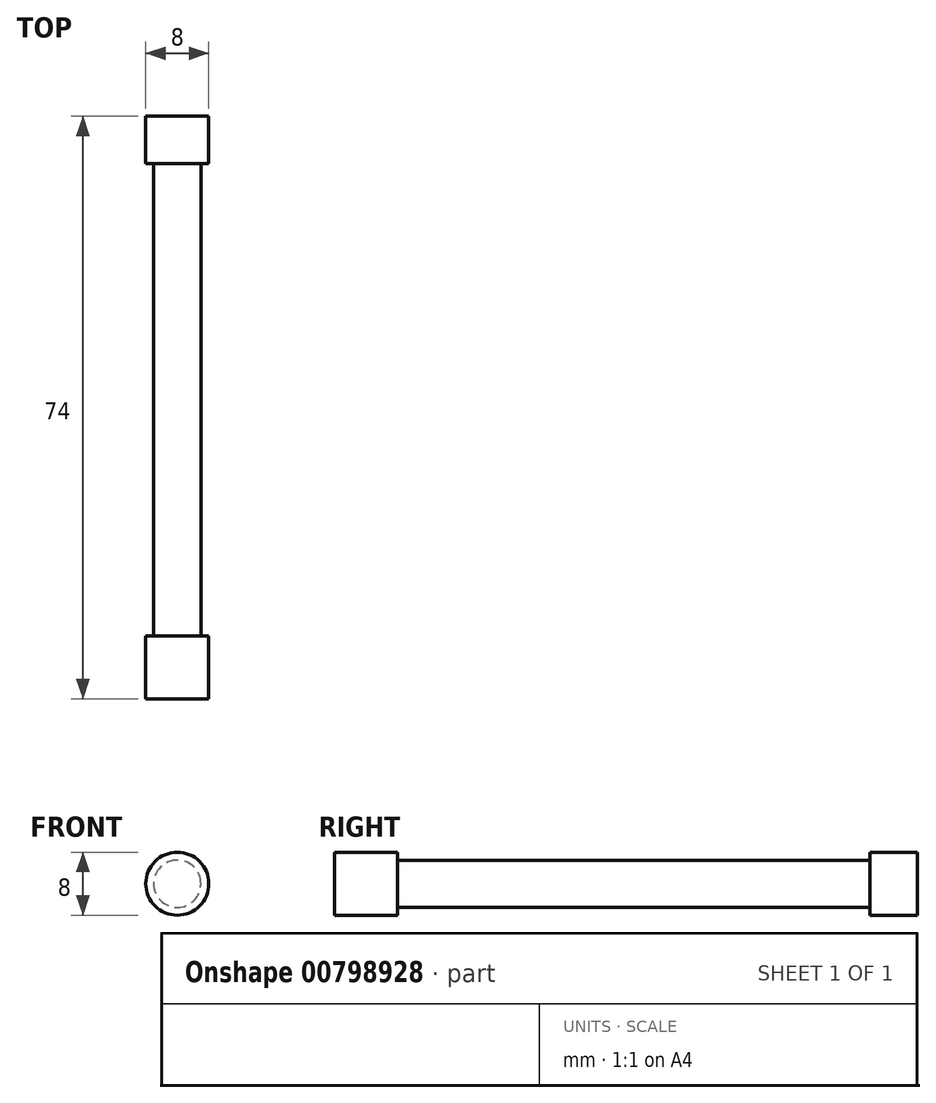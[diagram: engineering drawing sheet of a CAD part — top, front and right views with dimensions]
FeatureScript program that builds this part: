
annotation { "Feature Type Name" : "Feature", "Feature Type Description" : "" }
export const myFeature = defineFeature(function(context is Context, id is Id, definition is map)
    precondition{}
    {
        {
            var Q0;
            Q0=qCreatedBy(makeId("Front.planeOp"),FACE);
            var sketch = newSketch(context, id + "F0", { "sketchPlane" : qUnion([Q0])});
            skCircle(sketch, "E0", {"center": v(0, 0) * mm, "radius": 3 * mm});
            skSolve(sketch);
        }
        {
            var Q0;
            Q0=makeQuery(id+"F0.imprint","IMPRINT",FACE,{"disambiguationData":[TD([[makeQuery(id+"F0.imprint","IMPRINT",EDGE,{"derivedFrom":sQuery(id+"F0.wireOp",EDGE,"E0")}),1.0]])]});
            extrude(context, id + "F1", {"entities" : qUnion([Q0]), "endBound" : BoundingType.SYMMETRIC, "depth" : 60 * mm});
        }
        {
            var Q0;
            Q0=makeQuery(id+"F1.opExtrude","CAP_FACE",FACE,{"disambiguationData":[OSD([sQuery(id+"F0.wireOp",EDGE,"E0")])],"isStart":false});
            var sketch = newSketch(context, id + "F2", { "sketchPlane" : qUnion([Q0])});
            skCircle(sketch, "E1", {"center": v(0, 0) * mm, "radius": 4 * mm});
            skSolve(sketch);
        }
        {
            var Q0;
            Q0=makeQuery(id+"F1.opExtrude","CAP_FACE",FACE,{"disambiguationData":[OSD([sQuery(id+"F0.wireOp",EDGE,"E0")])],"isStart":true});
            var sketch = newSketch(context, id + "F3", { "sketchPlane" : qUnion([Q0])});
            skCircle(sketch, "E2", {"center": v(0, 0) * mm, "radius": 4 * mm});
            skSolve(sketch);
        }
        {
            var Q0;
            Q0=makeQuery(id+"F3.imprint","IMPRINT",FACE,{"disambiguationData":[TD([[makeQuery(id+"F3.imprint","IMPRINT",EDGE,{"derivedFrom":makeQuery(id+"F1.opExtrude","CAP_EDGE",EDGE,{"disambiguationData":[OSD([sQuery(id+"F0.wireOp",EDGE,"E0")])],"isStart":true})}),-1.0]])]});
            var Q1;
            Q1=makeQuery(id+"F3.imprint","IMPRINT",FACE,{"disambiguationData":[TD([[makeQuery(id+"F3.imprint","IMPRINT",EDGE,{"derivedFrom":sQuery(id+"F3.wireOp",EDGE,"E2")}),1.0]])]});
            extrude(context, id + "F4", {"entities" : qUnion([Q0, Q1]), "operationType" : NewBodyOperationType.ADD, "depth" : 6 * mm});
        }
        {
            var Q0;
            Q0=makeQuery(id+"F2.imprint","IMPRINT",FACE,{"disambiguationData":[TD([[makeQuery(id+"F2.imprint","IMPRINT",EDGE,{"derivedFrom":makeQuery(id+"F1.opExtrude","CAP_EDGE",EDGE,{"disambiguationData":[OSD([sQuery(id+"F0.wireOp",EDGE,"E0")])],"isStart":false})}),1.0]])]});
            var Q1;
            Q1=makeQuery(id+"F2.imprint","IMPRINT",FACE,{"disambiguationData":[TD([[makeQuery(id+"F2.imprint","IMPRINT",EDGE,{"derivedFrom":sQuery(id+"F2.wireOp",EDGE,"E1")}),1.0]])]});
            extrude(context, id + "F5", {"entities" : qUnion([Q0, Q1]), "operationType" : NewBodyOperationType.ADD, "depth" : 8 * mm});
        }
    });
